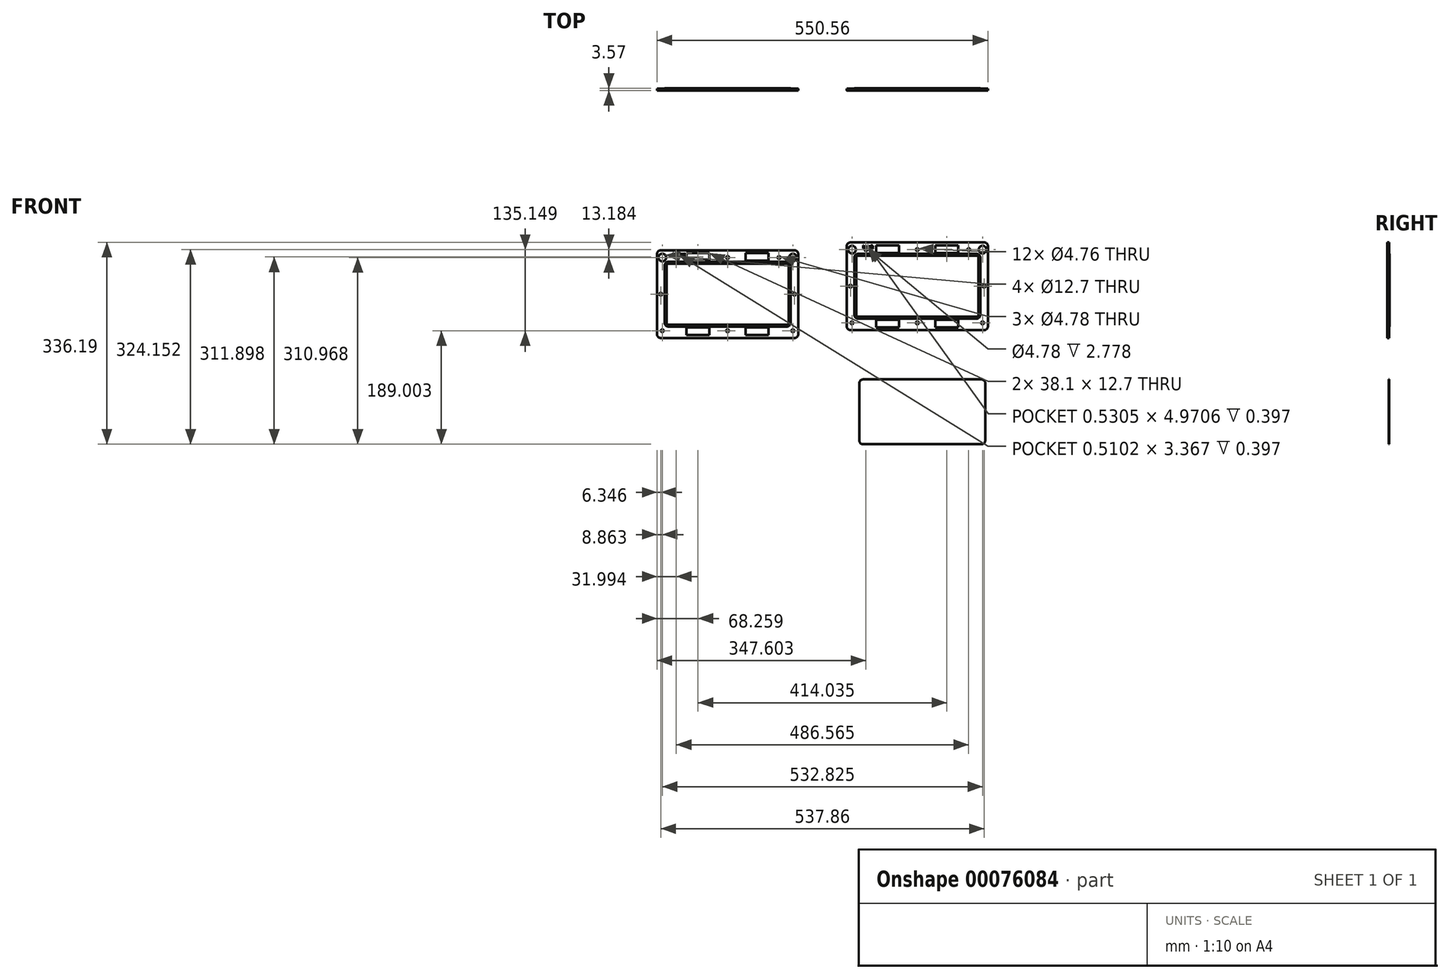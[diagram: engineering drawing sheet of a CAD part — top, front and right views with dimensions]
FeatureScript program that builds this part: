
annotation { "Feature Type Name" : "Feature", "Feature Type Description" : "" }
export const myFeature = defineFeature(function(context is Context, id is Id, definition is map)
    precondition{}
    {
        {
            var Q0;
            Q0=qCreatedBy(makeId("Front.planeOp"),FACE);
            var sketch = newSketch(context, id + "F0", { "sketchPlane" : qUnion([Q0])});
            skLineSegment(sketch, "E0.bottom", {"start": v(-85.43, 54.25) * mm, "end": v(111.42, 54.25) * mm});
            skLineSegment(sketch, "E0.top", {"start": v(-85.43, -53.7) * mm, "end": v(111.42, -53.7) * mm});
            skLineSegment(sketch, "E0.left", {"start": v(-91.78, 47.9) * mm, "end": v(-91.78, -47.35) * mm});
            skLineSegment(sketch, "E0.right", {"start": v(117.77, 47.9) * mm, "end": v(117.77, -47.35) * mm});
            skPoint(sketch, "E1.visualSharp", {"position": v(-91.78, 54.25) * mm});
            skArc(sketch, "E1.filletArc", {"start": v(-85.43, 54.25) * mm, "mid": v(-89.92, 52.4) * mm, "end": v(-91.78, 47.9) * mm});
            skPoint(sketch, "E2.visualSharp", {"position": v(117.77, 54.25) * mm});
            skArc(sketch, "E2.filletArc", {"start": v(117.77, 47.9) * mm, "mid": v(115.9, 52.4) * mm, "end": v(111.42, 54.25) * mm});
            skPoint(sketch, "E3.visualSharp", {"position": v(117.77, -53.7) * mm});
            skArc(sketch, "E3.filletArc", {"start": v(111.42, -53.7) * mm, "mid": v(115.9, -51.84) * mm, "end": v(117.77, -47.35) * mm});
            skPoint(sketch, "E4.visualSharp", {"position": v(-91.78, -53.7) * mm});
            skArc(sketch, "E4.filletArc", {"start": v(-91.78, -47.35) * mm, "mid": v(-89.92, -51.84) * mm, "end": v(-85.43, -53.7) * mm});
            skArc(sketch, "E5.0", {"start": v(-85.43, 51.08) * mm, "mid": v(-87.68, 50.15) * mm, "end": v(-88.6, 47.9) * mm});
            skLineSegment(sketch, "E5.1", {"start": v(-88.6, 47.9) * mm, "end": v(-88.6, -47.35) * mm});
            skLineSegment(sketch, "E5.2", {"start": v(-85.43, 51.08) * mm, "end": v(111.42, 51.08) * mm});
            skArc(sketch, "E5.3", {"start": v(-88.6, -47.35) * mm, "mid": v(-87.68, -49.6) * mm, "end": v(-85.43, -50.52) * mm});
            skArc(sketch, "E5.4", {"start": v(114.6, 47.9) * mm, "mid": v(113.66, 50.15) * mm, "end": v(111.42, 51.08) * mm});
            skLineSegment(sketch, "E5.5", {"start": v(114.6, 47.9) * mm, "end": v(114.6, -47.35) * mm});
            skArc(sketch, "E5.6", {"start": v(111.42, -50.52) * mm, "mid": v(113.66, -49.6) * mm, "end": v(114.6, -47.35) * mm});
            skLineSegment(sketch, "E5.7", {"start": v(-85.43, -50.52) * mm, "end": v(111.42, -50.52) * mm});
            skLineSegment(sketch, "E6.0", {"start": v(-98.13, 73.3) * mm, "end": v(124.12, 73.3) * mm});
            skLineSegment(sketch, "E7.0", {"start": v(-98.13, -72.75) * mm, "end": v(124.12, -72.75) * mm});
            skLineSegment(sketch, "E8.0", {"start": v(-104.48, 66.95) * mm, "end": v(-104.48, -66.4) * mm});
            skLineSegment(sketch, "E9.0", {"start": v(130.47, 66.95) * mm, "end": v(130.47, -66.4) * mm});
            skPoint(sketch, "E10.visualSharp", {"position": v(-104.48, 73.3) * mm});
            skArc(sketch, "E10.filletArc", {"start": v(-98.13, 73.3) * mm, "mid": v(-102.62, 71.44) * mm, "end": v(-104.48, 66.95) * mm});
            skPoint(sketch, "E11.visualSharp", {"position": v(130.47, 73.3) * mm});
            skArc(sketch, "E11.filletArc", {"start": v(130.47, 66.95) * mm, "mid": v(128.6, 71.44) * mm, "end": v(124.12, 73.3) * mm});
            skPoint(sketch, "E12.visualSharp", {"position": v(130.47, -72.75) * mm});
            skArc(sketch, "E12.filletArc", {"start": v(124.12, -72.75) * mm, "mid": v(128.6, -70.89) * mm, "end": v(130.47, -66.4) * mm});
            skPoint(sketch, "E13.visualSharp", {"position": v(-104.48, -72.75) * mm});
            skArc(sketch, "E13.filletArc", {"start": v(-104.48, -66.4) * mm, "mid": v(-102.62, -70.89) * mm, "end": v(-98.13, -72.75) * mm});
            skLineSegment(sketch, "E14", {"start": v(-104.48, 66.95) * mm, "end": v(-98.13, 73.3) * mm, "construction": true});
            skLineSegment(sketch, "E15", {"start": v(-101.3, 70.13) * mm, "end": v(-89.92, 52.4) * mm, "construction": true});
            skLineSegment(sketch, "E16", {"start": v(-104.48, 0.28) * mm, "end": v(-91.78, 0.28) * mm, "construction": true});
            skLineSegment(sketch, "E17", {"start": v(-98.13, -72.75) * mm, "end": v(-104.48, -66.4) * mm, "construction": true});
            skLineSegment(sketch, "E18", {"start": v(-101.3, -69.57) * mm, "end": v(-89.92, -51.84) * mm, "construction": true});
            skLineSegment(sketch, "E19", {"start": v(13, 94.6) * mm, "end": v(13, -140.03) * mm, "construction": true});
            skPoint(sketch, "E19.startSnap0", {"position": v(13, 73.3) * mm});
            skLineSegment(sketch, "E20", {"start": v(-149.83, 0.28) * mm, "end": v(205.44, 0.28) * mm, "construction": true});
            skLineSegment(sketch, "E21", {"start": v(-85.43, 54.25) * mm, "end": v(-85.43, 73.3) * mm, "construction": true});
            skCircle(sketch, "E22", {"center": v(-95.62, 61.26) * mm, "radius": 6.35 * mm});
            skCircle(sketch, "E23", {"center": v(-98.13, 0.28) * mm, "radius": 2.38 * mm});
            skCircle(sketch, "E24", {"center": v(-95.62, -60.7) * mm, "radius": 2.38 * mm});
            skLineSegment(sketch, "E25", {"start": v(-85.43, -53.7) * mm, "end": v(-85.43, -72.75) * mm, "construction": true});
            skLineSegment(sketch, "E26", {"start": v(-85.43, -72.75) * mm, "end": v(-85.43, -63.22) * mm, "construction": true});
            skLineSegment(sketch, "E27", {"start": v(-85.43, -63.22) * mm, "end": v(39.92, -63.22) * mm, "construction": true});
            skLineSegment(sketch, "E28", {"start": v(13, 54.25) * mm, "end": v(13, 73.3) * mm, "construction": true});
            skLineSegment(sketch, "E29", {"start": v(13, -72.75) * mm, "end": v(13, -53.7) * mm, "construction": true});
            skCircle(sketch, "E30", {"center": v(13, 61.26) * mm, "radius": 2.38 * mm});
            skLineSegment(sketch, "E31.bottom", {"start": v(-17.17, 55.84) * mm, "end": v(-55.27, 55.84) * mm});
            skLineSegment(sketch, "E31.top", {"start": v(-17.17, 68.54) * mm, "end": v(-55.27, 68.54) * mm});
            skLineSegment(sketch, "E31.left", {"start": v(-17.17, 55.84) * mm, "end": v(-17.17, 68.54) * mm});
            skLineSegment(sketch, "E31.right", {"start": v(-55.27, 55.84) * mm, "end": v(-55.27, 68.54) * mm});
            skPoint(sketch, "E31.middle", {"position": v(-36.22, 62.2) * mm});
            skLineSegment(sketch, "E32.MirrorCS", {"start": v(43.15, 55.84) * mm, "end": v(43.15, 68.54) * mm});
            skLineSegment(sketch, "E33.MirrorCS", {"start": v(43.15, 68.54) * mm, "end": v(81.25, 68.54) * mm});
            skLineSegment(sketch, "E34.MirrorCS", {"start": v(81.25, 55.84) * mm, "end": v(81.25, 68.54) * mm});
            skLineSegment(sketch, "E35.MirrorCS", {"start": v(43.15, 55.84) * mm, "end": v(81.25, 55.84) * mm});
            skCircle(sketch, "E36.MirrorC", {"center": v(121.6, 61.26) * mm, "radius": 6.35 * mm});
            skCircle(sketch, "E37.MirrorC", {"center": v(124.12, 0.28) * mm, "radius": 2.38 * mm});
            skCircle(sketch, "E38.MirrorC", {"center": v(121.6, -60.7) * mm, "radius": 2.38 * mm});
            skLineSegment(sketch, "E39.MirrorCS", {"start": v(-55.27, -55.28) * mm, "end": v(-55.27, -67.98) * mm});
            skLineSegment(sketch, "E40.MirrorCS", {"start": v(-17.17, -55.28) * mm, "end": v(-17.17, -67.98) * mm});
            skLineSegment(sketch, "E41.MirrorCS", {"start": v(-17.17, -55.28) * mm, "end": v(-55.27, -55.28) * mm});
            skLineSegment(sketch, "E42.MirrorCS", {"start": v(-17.17, -67.98) * mm, "end": v(-55.27, -67.98) * mm});
            skCircle(sketch, "E43.MirrorC", {"center": v(13, -60.7) * mm, "radius": 2.38 * mm});
            skLineSegment(sketch, "E44.MirrorCS", {"start": v(43.15, -55.28) * mm, "end": v(43.15, -67.98) * mm});
            skLineSegment(sketch, "E45.MirrorCS", {"start": v(43.15, -67.98) * mm, "end": v(81.25, -67.98) * mm});
            skLineSegment(sketch, "E46.MirrorCS", {"start": v(81.25, -55.28) * mm, "end": v(81.25, -67.98) * mm});
            skLineSegment(sketch, "E47.MirrorCS", {"start": v(43.15, -55.28) * mm, "end": v(81.25, -55.28) * mm});
            skLineSegment(sketch, "E48", {"start": v(-95.62, 61.26) * mm, "end": v(121.6, 61.26) * mm, "construction": true});
            skCircle(sketch, "E49", {"center": v(-72.49, 61.26) * mm, "radius": 2.39 * mm});
            skCircle(sketch, "E50", {"center": v(98.47, 61.26) * mm, "radius": 2.39 * mm});
            skSolve(sketch);
        }
        {
            var Q0;
            Q0 = qSketchRegion(id + "F0", true);
            var Q1;
            Q1=makeQuery(id+"F0.imprint","IMPRINT",FACE,{"disambiguationData":[TD([[makeQuery(id+"F0.imprint","IMPRINT",EDGE,{"derivedFrom":sQuery(id+"F0.wireOp",EDGE,"E0.bottom")}),-1.0]])]});
            extrude(context, id + "F1", {"entities" : qUnion([Q0, Q1]), "depth" : 0.8 * mm});
        }
        {
            var Q0;
            Q0=makeQuery(id+"F1.opExtrude","CAP_FACE",FACE,{"disambiguationData":[OSD([sQuery(id+"F0.wireOp",EDGE,"E5.0"),sQuery(id+"F0.wireOp",EDGE,"E5.1"),sQuery(id+"F0.wireOp",EDGE,"E5.2"),sQuery(id+"F0.wireOp",EDGE,"E5.3"),sQuery(id+"F0.wireOp",EDGE,"E5.4"),sQuery(id+"F0.wireOp",EDGE,"E5.5"),sQuery(id+"F0.wireOp",EDGE,"E5.6"),sQuery(id+"F0.wireOp",EDGE,"E5.7"),sQuery(id+"F0.wireOp",EDGE,"E6.0"),sQuery(id+"F0.wireOp",EDGE,"E7.0"),sQuery(id+"F0.wireOp",EDGE,"E8.0"),sQuery(id+"F0.wireOp",EDGE,"E9.0"),sQuery(id+"F0.wireOp",EDGE,"E10.filletArc"),sQuery(id+"F0.wireOp",EDGE,"E11.filletArc"),sQuery(id+"F0.wireOp",EDGE,"E12.filletArc"),sQuery(id+"F0.wireOp",EDGE,"E13.filletArc"),sQuery(id+"F0.wireOp",EDGE,"E22"),sQuery(id+"F0.wireOp",EDGE,"E23"),sQuery(id+"F0.wireOp",EDGE,"E24"),sQuery(id+"F0.wireOp",EDGE,"E30"),sQuery(id+"F0.wireOp",EDGE,"E31.bottom"),sQuery(id+"F0.wireOp",EDGE,"E31.top"),sQuery(id+"F0.wireOp",EDGE,"E31.left"),sQuery(id+"F0.wireOp",EDGE,"E31.right"),sQuery(id+"F0.wireOp",EDGE,"E32.MirrorCS"),sQuery(id+"F0.wireOp",EDGE,"E33.MirrorCS"),sQuery(id+"F0.wireOp",EDGE,"E34.MirrorCS"),sQuery(id+"F0.wireOp",EDGE,"E35.MirrorCS"),sQuery(id+"F0.wireOp",EDGE,"E36.MirrorC"),sQuery(id+"F0.wireOp",EDGE,"E37.MirrorC"),sQuery(id+"F0.wireOp",EDGE,"E38.MirrorC"),sQuery(id+"F0.wireOp",EDGE,"E39.MirrorCS"),sQuery(id+"F0.wireOp",EDGE,"E40.MirrorCS"),sQuery(id+"F0.wireOp",EDGE,"E41.MirrorCS"),sQuery(id+"F0.wireOp",EDGE,"E42.MirrorCS"),sQuery(id+"F0.wireOp",EDGE,"E43.MirrorC"),sQuery(id+"F0.wireOp",EDGE,"E44.MirrorCS"),sQuery(id+"F0.wireOp",EDGE,"E45.MirrorCS"),sQuery(id+"F0.wireOp",EDGE,"E46.MirrorCS"),sQuery(id+"F0.wireOp",EDGE,"E47.MirrorCS")])],"isStart":false});
            var sketch = newSketch(context, id + "F2", { "sketchPlane" : qUnion([Q0])});
            skLineSegment(sketch, "E51.0", {"start": v(-85.43, 54.25) * mm, "end": v(111.42, 54.25) * mm});
            skLineSegment(sketch, "E52.0", {"start": v(-85.43, -53.7) * mm, "end": v(111.42, -53.7) * mm});
            skLineSegment(sketch, "E53", {"start": v(-91.78, 47.9) * mm, "end": v(-91.78, -47.35) * mm});
            skLineSegment(sketch, "E54", {"start": v(117.77, 47.9) * mm, "end": v(117.77, -47.35) * mm});
            skPoint(sketch, "E55.visualSharp", {"position": v(-91.78, 54.25) * mm});
            skArc(sketch, "E55.filletArc", {"start": v(-85.43, 54.25) * mm, "mid": v(-89.92, 52.4) * mm, "end": v(-91.78, 47.9) * mm});
            skPoint(sketch, "E56.visualSharp", {"position": v(117.77, 54.25) * mm});
            skArc(sketch, "E56.filletArc", {"start": v(117.77, 47.9) * mm, "mid": v(115.9, 52.4) * mm, "end": v(111.42, 54.25) * mm});
            skPoint(sketch, "E57.visualSharp", {"position": v(117.77, -53.7) * mm});
            skArc(sketch, "E57.filletArc", {"start": v(111.42, -53.7) * mm, "mid": v(115.9, -51.84) * mm, "end": v(117.77, -47.35) * mm});
            skPoint(sketch, "E58.visualSharp", {"position": v(-91.78, -53.7) * mm});
            skArc(sketch, "E58.filletArc", {"start": v(-91.78, -47.35) * mm, "mid": v(-89.92, -51.84) * mm, "end": v(-85.43, -53.7) * mm});
            skSolve(sketch);
        }
        {
            var Q0;
            Q0=makeQuery(id+"F2.imprint","IMPRINT",FACE,{"disambiguationData":[TD([[makeQuery(id+"F2.imprint","IMPRINT",EDGE,{"derivedFrom":sQuery(id+"F2.wireOp",EDGE,"E51.0")}),1.0]])]});
            extrude(context, id + "F3", {"entities" : qUnion([Q0]), "operationType" : NewBodyOperationType.ADD, "depth" : 1.98 * mm});
        }
        {
            var Q0;
            Q0=qCreatedBy(makeId("Front.planeOp"),FACE);
            var sketch = newSketch(context, id + "F4", { "sketchPlane" : qUnion([Q0])});
            skLineSegment(sketch, "E59.bottom", {"start": v(-77.21, -154.94) * mm, "end": v(119.64, -154.94) * mm});
            skLineSegment(sketch, "E59.top", {"start": v(-77.21, -262.89) * mm, "end": v(119.64, -262.89) * mm});
            skLineSegment(sketch, "E59.left", {"start": v(-83.56, -161.29) * mm, "end": v(-83.56, -256.54) * mm});
            skLineSegment(sketch, "E59.right", {"start": v(125.99, -161.29) * mm, "end": v(125.99, -256.54) * mm});
            skPoint(sketch, "E60.visualSharp", {"position": v(-83.56, -154.94) * mm});
            skArc(sketch, "E60.filletArc", {"start": v(-77.21, -154.94) * mm, "mid": v(-81.7, -156.8) * mm, "end": v(-83.56, -161.29) * mm});
            skPoint(sketch, "E61.visualSharp", {"position": v(125.99, -154.94) * mm});
            skArc(sketch, "E61.filletArc", {"start": v(125.99, -161.29) * mm, "mid": v(124.13, -156.8) * mm, "end": v(119.64, -154.94) * mm});
            skPoint(sketch, "E62.visualSharp", {"position": v(-83.56, -262.89) * mm});
            skArc(sketch, "E62.filletArc", {"start": v(-83.56, -256.54) * mm, "mid": v(-81.7, -261.03) * mm, "end": v(-77.21, -262.89) * mm});
            skPoint(sketch, "E63.visualSharp", {"position": v(125.99, -262.89) * mm});
            skArc(sketch, "E63.filletArc", {"start": v(119.64, -262.89) * mm, "mid": v(124.13, -261.03) * mm, "end": v(125.99, -256.54) * mm});
            skSolve(sketch);
        }
        {
            var Q0;
            Q0 = qSketchRegion(id + "F4", true);
            extrude(context, id + "F5", {"entities" : qUnion([Q0]), "depth" : 0.4 * mm});
        }
        {
            var Q0;
            Q0=makeQuery(id+"F1.opExtrude","CAP_FACE",FACE,{"disambiguationData":[OSD([sQuery(id+"F0.wireOp",EDGE,"E5.0"),sQuery(id+"F0.wireOp",EDGE,"E5.1"),sQuery(id+"F0.wireOp",EDGE,"E5.2"),sQuery(id+"F0.wireOp",EDGE,"E5.3"),sQuery(id+"F0.wireOp",EDGE,"E5.4"),sQuery(id+"F0.wireOp",EDGE,"E5.5"),sQuery(id+"F0.wireOp",EDGE,"E5.6"),sQuery(id+"F0.wireOp",EDGE,"E5.7"),sQuery(id+"F0.wireOp",EDGE,"E6.0"),sQuery(id+"F0.wireOp",EDGE,"E7.0"),sQuery(id+"F0.wireOp",EDGE,"E8.0"),sQuery(id+"F0.wireOp",EDGE,"E9.0"),sQuery(id+"F0.wireOp",EDGE,"E10.filletArc"),sQuery(id+"F0.wireOp",EDGE,"E11.filletArc"),sQuery(id+"F0.wireOp",EDGE,"E12.filletArc"),sQuery(id+"F0.wireOp",EDGE,"E13.filletArc"),sQuery(id+"F0.wireOp",EDGE,"E22"),sQuery(id+"F0.wireOp",EDGE,"E23"),sQuery(id+"F0.wireOp",EDGE,"E24"),sQuery(id+"F0.wireOp",EDGE,"E30"),sQuery(id+"F0.wireOp",EDGE,"E31.bottom"),sQuery(id+"F0.wireOp",EDGE,"E31.top"),sQuery(id+"F0.wireOp",EDGE,"E31.left"),sQuery(id+"F0.wireOp",EDGE,"E31.right"),sQuery(id+"F0.wireOp",EDGE,"E32.MirrorCS"),sQuery(id+"F0.wireOp",EDGE,"E33.MirrorCS"),sQuery(id+"F0.wireOp",EDGE,"E34.MirrorCS"),sQuery(id+"F0.wireOp",EDGE,"E35.MirrorCS"),sQuery(id+"F0.wireOp",EDGE,"E36.MirrorC"),sQuery(id+"F0.wireOp",EDGE,"E37.MirrorC"),sQuery(id+"F0.wireOp",EDGE,"E38.MirrorC"),sQuery(id+"F0.wireOp",EDGE,"E39.MirrorCS"),sQuery(id+"F0.wireOp",EDGE,"E40.MirrorCS"),sQuery(id+"F0.wireOp",EDGE,"E41.MirrorCS"),sQuery(id+"F0.wireOp",EDGE,"E42.MirrorCS"),sQuery(id+"F0.wireOp",EDGE,"E43.MirrorC"),sQuery(id+"F0.wireOp",EDGE,"E44.MirrorCS"),sQuery(id+"F0.wireOp",EDGE,"E45.MirrorCS"),sQuery(id+"F0.wireOp",EDGE,"E46.MirrorCS"),sQuery(id+"F0.wireOp",EDGE,"E47.MirrorCS")])],"isStart":true});
            var sketch = newSketch(context, id + "F6", { "sketchPlane" : qUnion([Q0])});
            skLineSegment(sketch, "E64.0", {"start": v(85.43, 54.25) * mm, "end": v(55.27, 54.25) * mm});
            skArc(sketch, "E64.1", {"start": v(85.43, 54.25) * mm, "mid": v(89.92, 52.4) * mm, "end": v(91.78, 47.9) * mm});
            skLineSegment(sketch, "E64.2", {"start": v(91.78, 47.9) * mm, "end": v(91.78, -47.35) * mm});
            skArc(sketch, "E64.3", {"start": v(91.78, -47.35) * mm, "mid": v(89.92, -51.84) * mm, "end": v(85.43, -53.7) * mm});
            skLineSegment(sketch, "E64.4", {"start": v(85.43, -53.7) * mm, "end": v(-111.42, -53.7) * mm});
            skLineSegment(sketch, "E64.5", {"start": v(17.17, 54.25) * mm, "end": v(-111.42, 54.25) * mm});
            skArc(sketch, "E64.6", {"start": v(-117.77, 47.9) * mm, "mid": v(-115.9, 52.4) * mm, "end": v(-111.42, 54.25) * mm});
            skLineSegment(sketch, "E64.7", {"start": v(-117.77, 47.9) * mm, "end": v(-117.77, -47.35) * mm});
            skArc(sketch, "E64.8", {"start": v(-111.42, -53.7) * mm, "mid": v(-115.9, -51.84) * mm, "end": v(-117.77, -47.35) * mm});
            skLineSegment(sketch, "E65", {"start": v(17.17, 54.25) * mm, "end": v(55.27, 54.25) * mm});
            skArc(sketch, "E66.0", {"start": v(85.43, 51.08) * mm, "mid": v(87.68, 50.15) * mm, "end": v(88.6, 47.9) * mm});
            skLineSegment(sketch, "E66.1", {"start": v(88.6, 47.9) * mm, "end": v(88.6, -47.35) * mm});
            skLineSegment(sketch, "E66.2", {"start": v(85.43, 51.08) * mm, "end": v(-111.42, 51.08) * mm});
            skArc(sketch, "E66.3", {"start": v(88.6, -47.35) * mm, "mid": v(87.68, -49.6) * mm, "end": v(85.43, -50.52) * mm});
            skArc(sketch, "E66.4", {"start": v(-114.6, 47.9) * mm, "mid": v(-113.66, 50.15) * mm, "end": v(-111.42, 51.08) * mm});
            skLineSegment(sketch, "E66.5", {"start": v(-114.6, 47.9) * mm, "end": v(-114.6, -47.35) * mm});
            skArc(sketch, "E66.6", {"start": v(-111.42, -50.52) * mm, "mid": v(-113.66, -49.6) * mm, "end": v(-114.6, -47.35) * mm});
            skLineSegment(sketch, "E66.7", {"start": v(85.43, -50.52) * mm, "end": v(-111.42, -50.52) * mm});
            skSolve(sketch);
        }
        {
            var Q0;
            Q0 = qSketchRegion(id + "F6", true);
            extrude(context, id + "F7", {"entities" : qUnion([Q0]), "operationType" : NewBodyOperationType.ADD, "depth" : 0.8 * mm});
        }
        {
            var Q0;
            Q0=makeQuery(id+"F0.imprint","IMPRINT",FACE,{"disambiguationData":[TD([[makeQuery(id+"F0.imprint","IMPRINT",EDGE,{"derivedFrom":sQuery(id+"F0.wireOp",EDGE,"E0.bottom")}),1.0]])]});
            var sketch = newSketch(context, id + "F8", { "sketchPlane" : qUnion([Q0])});
            skLineSegment(sketch, "E67.bottom", {"start": v(-17.17, 55.84) * mm, "end": v(-55.3, 55.84) * mm});
            skLineSegment(sketch, "E67.top", {"start": v(-17.17, 50.55) * mm, "end": v(-55.3, 50.55) * mm});
            skLineSegment(sketch, "E67.left", {"start": v(-17.17, 55.84) * mm, "end": v(-17.17, 50.55) * mm});
            skLineSegment(sketch, "E67.right", {"start": v(-55.3, 55.84) * mm, "end": v(-55.3, 50.55) * mm});
            skLineSegment(sketch, "E68.MirrorCS", {"start": v(-17.17, -55.28) * mm, "end": v(-55.3, -55.28) * mm});
            skLineSegment(sketch, "E69.MirrorCS", {"start": v(-17.17, -55.28) * mm, "end": v(-17.17, -49.99) * mm});
            skLineSegment(sketch, "E70.MirrorCS", {"start": v(-17.17, -49.99) * mm, "end": v(-55.3, -49.99) * mm});
            skLineSegment(sketch, "E71.MirrorCS", {"start": v(-55.3, -55.28) * mm, "end": v(-55.3, -49.99) * mm});
            skLineSegment(sketch, "E72.MirrorCS", {"start": v(43.15, -55.28) * mm, "end": v(43.15, -49.99) * mm});
            skLineSegment(sketch, "E73.MirrorCS", {"start": v(43.15, -49.99) * mm, "end": v(81.27, -49.99) * mm});
            skLineSegment(sketch, "E74.MirrorCS", {"start": v(43.15, -55.28) * mm, "end": v(81.27, -55.28) * mm});
            skLineSegment(sketch, "E75.MirrorCS", {"start": v(81.27, -55.28) * mm, "end": v(81.27, -49.99) * mm});
            skSolve(sketch);
        }
        {
            var Q0;
            Q0 = qSketchRegion(id + "F8", true);
            extrude(context, id + "F9", {"entities" : qUnion([Q0]), "operationType" : NewBodyOperationType.REMOVE, "depth" : 0.8 * mm});
        }
        {
            var Q0;
            Q0=makeQuery(id+"F3.opExtrude","CAP_FACE",FACE,{"disambiguationData":[OSD([sQuery(id+"F0.wireOp",EDGE,"E6.0"),sQuery(id+"F0.wireOp",EDGE,"E7.0"),sQuery(id+"F0.wireOp",EDGE,"E8.0"),sQuery(id+"F0.wireOp",EDGE,"E9.0"),sQuery(id+"F0.wireOp",EDGE,"E10.filletArc"),sQuery(id+"F0.wireOp",EDGE,"E11.filletArc"),sQuery(id+"F0.wireOp",EDGE,"E12.filletArc"),sQuery(id+"F0.wireOp",EDGE,"E13.filletArc"),sQuery(id+"F0.wireOp",EDGE,"E22"),sQuery(id+"F0.wireOp",EDGE,"E23"),sQuery(id+"F0.wireOp",EDGE,"E24"),sQuery(id+"F0.wireOp",EDGE,"E30"),sQuery(id+"F0.wireOp",EDGE,"E31.bottom"),sQuery(id+"F0.wireOp",EDGE,"E31.top"),sQuery(id+"F0.wireOp",EDGE,"E31.left"),sQuery(id+"F0.wireOp",EDGE,"E31.right"),sQuery(id+"F0.wireOp",EDGE,"E32.MirrorCS"),sQuery(id+"F0.wireOp",EDGE,"E33.MirrorCS"),sQuery(id+"F0.wireOp",EDGE,"E34.MirrorCS"),sQuery(id+"F0.wireOp",EDGE,"E35.MirrorCS"),sQuery(id+"F0.wireOp",EDGE,"E36.MirrorC"),sQuery(id+"F0.wireOp",EDGE,"E37.MirrorC"),sQuery(id+"F0.wireOp",EDGE,"E38.MirrorC"),sQuery(id+"F0.wireOp",EDGE,"E39.MirrorCS"),sQuery(id+"F0.wireOp",EDGE,"E40.MirrorCS"),sQuery(id+"F0.wireOp",EDGE,"E41.MirrorCS"),sQuery(id+"F0.wireOp",EDGE,"E42.MirrorCS"),sQuery(id+"F0.wireOp",EDGE,"E43.MirrorC"),sQuery(id+"F0.wireOp",EDGE,"E44.MirrorCS"),sQuery(id+"F0.wireOp",EDGE,"E45.MirrorCS"),sQuery(id+"F0.wireOp",EDGE,"E46.MirrorCS"),sQuery(id+"F0.wireOp",EDGE,"E47.MirrorCS"),sQuery(id+"F2.wireOp",EDGE,"E51.0"),sQuery(id+"F2.wireOp",EDGE,"E52.0"),sQuery(id+"F2.wireOp",EDGE,"E53"),sQuery(id+"F2.wireOp",EDGE,"E54"),sQuery(id+"F2.wireOp",EDGE,"E55.filletArc"),sQuery(id+"F2.wireOp",EDGE,"E56.filletArc"),sQuery(id+"F2.wireOp",EDGE,"E57.filletArc"),sQuery(id+"F2.wireOp",EDGE,"E58.filletArc")])],"isStart":false});
            var sketch = newSketch(context, id + "F10", { "sketchPlane" : qUnion([Q0])});
            skText(sketch, "E76", { "text": "M left", "fontName": "OpenSans-Regular.ttf"});
            const initialGuessF10  = {"E76": [-0.07783, 0.06345, 1, 0, 0.00471]};
            skSetInitialGuess(sketch, initialGuessF10);
            skSolve(sketch);
        }
        {
            var Q0;
            Q0 = qSketchRegion(id + "F10", true);
            extrude(context, id + "F11", {"entities" : qUnion([Q0]), "operationType" : NewBodyOperationType.REMOVE, "oppositeDirection" : true, "depth" : 0.4 * mm});
        }
        {
            var Q0;
            Q0=qCreatedBy(makeId("Front.planeOp"),FACE);
            var sketch = newSketch(context, id + "F12", { "sketchPlane" : qUnion([Q0])});
            skLineSegment(sketch, "E77.bottom", {"start": v(-401.04, 41.07) * mm, "end": v(-204.2, 41.07) * mm});
            skLineSegment(sketch, "E77.top", {"start": v(-401.04, -66.88) * mm, "end": v(-204.2, -66.88) * mm});
            skLineSegment(sketch, "E77.left", {"start": v(-407.4, 34.72) * mm, "end": v(-407.4, -60.53) * mm});
            skLineSegment(sketch, "E77.right", {"start": v(-197.84, 34.72) * mm, "end": v(-197.84, -60.53) * mm});
            skPoint(sketch, "E78.visualSharp", {"position": v(-407.4, 41.07) * mm});
            skArc(sketch, "E78.filletArc", {"start": v(-401.04, 41.07) * mm, "mid": v(-405.53, 39.21) * mm, "end": v(-407.4, 34.72) * mm});
            skPoint(sketch, "E79.visualSharp", {"position": v(-197.84, 41.07) * mm});
            skArc(sketch, "E79.filletArc", {"start": v(-197.84, 34.72) * mm, "mid": v(-199.7, 39.21) * mm, "end": v(-204.2, 41.07) * mm});
            skPoint(sketch, "E80.visualSharp", {"position": v(-197.84, -66.88) * mm});
            skArc(sketch, "E80.filletArc", {"start": v(-204.2, -66.88) * mm, "mid": v(-199.7, -65.02) * mm, "end": v(-197.84, -60.53) * mm});
            skPoint(sketch, "E81.visualSharp", {"position": v(-407.4, -66.88) * mm});
            skArc(sketch, "E81.filletArc", {"start": v(-407.4, -60.53) * mm, "mid": v(-405.53, -65.02) * mm, "end": v(-401.04, -66.88) * mm});
            skArc(sketch, "E82.0", {"start": v(-401.04, 37.9) * mm, "mid": v(-403.29, 36.97) * mm, "end": v(-404.22, 34.72) * mm});
            skLineSegment(sketch, "E82.1", {"start": v(-404.22, 34.72) * mm, "end": v(-404.22, -60.53) * mm});
            skLineSegment(sketch, "E82.2", {"start": v(-401.04, 37.9) * mm, "end": v(-204.2, 37.9) * mm});
            skArc(sketch, "E82.3", {"start": v(-404.22, -60.53) * mm, "mid": v(-403.29, -62.77) * mm, "end": v(-401.04, -63.7) * mm});
            skArc(sketch, "E82.4", {"start": v(-201.02, 34.72) * mm, "mid": v(-201.95, 36.97) * mm, "end": v(-204.2, 37.9) * mm});
            skLineSegment(sketch, "E82.5", {"start": v(-201.02, 34.72) * mm, "end": v(-201.02, -60.53) * mm});
            skArc(sketch, "E82.6", {"start": v(-204.2, -63.7) * mm, "mid": v(-201.95, -62.77) * mm, "end": v(-201.02, -60.53) * mm});
            skLineSegment(sketch, "E82.7", {"start": v(-401.04, -63.7) * mm, "end": v(-204.2, -63.7) * mm});
            skLineSegment(sketch, "E83.0", {"start": v(-413.74, 60.12) * mm, "end": v(-191.5, 60.12) * mm});
            skLineSegment(sketch, "E84.0", {"start": v(-413.74, -85.93) * mm, "end": v(-191.5, -85.93) * mm});
            skLineSegment(sketch, "E85.0", {"start": v(-420.1, 53.77) * mm, "end": v(-420.1, -79.58) * mm});
            skLineSegment(sketch, "E86.0", {"start": v(-185.14, 53.77) * mm, "end": v(-185.14, -79.58) * mm});
            skPoint(sketch, "E87.visualSharp", {"position": v(-420.1, 60.12) * mm});
            skArc(sketch, "E87.filletArc", {"start": v(-413.74, 60.12) * mm, "mid": v(-418.23, 58.26) * mm, "end": v(-420.1, 53.77) * mm});
            skPoint(sketch, "E88.visualSharp", {"position": v(-185.14, 60.12) * mm});
            skArc(sketch, "E88.filletArc", {"start": v(-185.14, 53.77) * mm, "mid": v(-187, 58.26) * mm, "end": v(-191.5, 60.12) * mm});
            skPoint(sketch, "E89.visualSharp", {"position": v(-185.14, -85.93) * mm});
            skArc(sketch, "E89.filletArc", {"start": v(-191.5, -85.93) * mm, "mid": v(-187, -84.07) * mm, "end": v(-185.14, -79.58) * mm});
            skPoint(sketch, "E90.visualSharp", {"position": v(-420.1, -85.93) * mm});
            skArc(sketch, "E90.filletArc", {"start": v(-420.1, -79.58) * mm, "mid": v(-418.23, -84.07) * mm, "end": v(-413.74, -85.93) * mm});
            skLineSegment(sketch, "E91", {"start": v(-420.1, 53.77) * mm, "end": v(-413.74, 60.12) * mm, "construction": true});
            skLineSegment(sketch, "E92", {"start": v(-416.92, 56.95) * mm, "end": v(-405.53, 39.21) * mm, "construction": true});
            skLineSegment(sketch, "E93", {"start": v(-420.1, -12.9) * mm, "end": v(-407.4, -12.9) * mm, "construction": true});
            skLineSegment(sketch, "E94", {"start": v(-413.74, -85.93) * mm, "end": v(-420.1, -79.58) * mm, "construction": true});
            skLineSegment(sketch, "E95", {"start": v(-416.92, -82.75) * mm, "end": v(-405.53, -65.02) * mm, "construction": true});
            skLineSegment(sketch, "E96", {"start": v(-302.62, 81.4) * mm, "end": v(-302.62, -153.21) * mm, "construction": true});
            skPoint(sketch, "E96.startSnap0", {"position": v(-302.62, 60.12) * mm});
            skLineSegment(sketch, "E97", {"start": v(-465.44, -12.9) * mm, "end": v(-110.17, -12.9) * mm, "construction": true});
            skLineSegment(sketch, "E98", {"start": v(-401.04, 41.07) * mm, "end": v(-401.04, 60.12) * mm, "construction": true});
            skCircle(sketch, "E99", {"center": v(-411.23, 48.08) * mm, "radius": 6.35 * mm});
            skCircle(sketch, "E100", {"center": v(-413.74, -12.9) * mm, "radius": 2.38 * mm});
            skCircle(sketch, "E101", {"center": v(-411.23, -73.89) * mm, "radius": 2.38 * mm});
            skLineSegment(sketch, "E102", {"start": v(-401.04, -66.88) * mm, "end": v(-401.04, -85.93) * mm, "construction": true});
            skLineSegment(sketch, "E103", {"start": v(-401.04, -85.93) * mm, "end": v(-401.04, -76.4) * mm, "construction": true});
            skLineSegment(sketch, "E104", {"start": v(-401.04, -76.4) * mm, "end": v(-275.69, -76.4) * mm, "construction": true});
            skLineSegment(sketch, "E105", {"start": v(-302.62, 41.07) * mm, "end": v(-302.62, 60.12) * mm, "construction": true});
            skLineSegment(sketch, "E106", {"start": v(-302.62, -85.93) * mm, "end": v(-302.62, -66.88) * mm, "construction": true});
            skCircle(sketch, "E107", {"center": v(-302.61, 48.08) * mm, "radius": 2.38 * mm});
            skLineSegment(sketch, "E108.bottom", {"start": v(-332.78, 42.66) * mm, "end": v(-370.88, 42.66) * mm});
            skLineSegment(sketch, "E108.top", {"start": v(-332.78, 55.36) * mm, "end": v(-370.88, 55.36) * mm});
            skLineSegment(sketch, "E108.left", {"start": v(-332.78, 42.66) * mm, "end": v(-332.78, 55.36) * mm});
            skLineSegment(sketch, "E108.right", {"start": v(-370.88, 42.66) * mm, "end": v(-370.88, 55.36) * mm});
            skPoint(sketch, "E108.middle", {"position": v(-351.83, 49) * mm});
            skLineSegment(sketch, "E109.MirrorCS", {"start": v(-272.46, 42.66) * mm, "end": v(-272.46, 55.36) * mm});
            skLineSegment(sketch, "E110.MirrorCS", {"start": v(-272.46, 55.36) * mm, "end": v(-234.36, 55.36) * mm});
            skLineSegment(sketch, "E111.MirrorCS", {"start": v(-234.36, 42.66) * mm, "end": v(-234.36, 55.36) * mm});
            skLineSegment(sketch, "E112.MirrorCS", {"start": v(-272.46, 42.66) * mm, "end": v(-234.36, 42.66) * mm});
            skCircle(sketch, "E113.MirrorC", {"center": v(-194.01, 48.08) * mm, "radius": 6.35 * mm});
            skCircle(sketch, "E114.MirrorC", {"center": v(-191.5, -12.9) * mm, "radius": 2.38 * mm});
            skCircle(sketch, "E115.MirrorC", {"center": v(-194.01, -73.89) * mm, "radius": 2.38 * mm});
            skLineSegment(sketch, "E116.MirrorCS", {"start": v(-370.88, -68.47) * mm, "end": v(-370.88, -81.17) * mm});
            skLineSegment(sketch, "E117.MirrorCS", {"start": v(-332.78, -68.47) * mm, "end": v(-332.78, -81.17) * mm});
            skLineSegment(sketch, "E118.MirrorCS", {"start": v(-332.78, -68.47) * mm, "end": v(-370.88, -68.47) * mm});
            skLineSegment(sketch, "E119.MirrorCS", {"start": v(-332.78, -81.17) * mm, "end": v(-370.88, -81.17) * mm});
            skCircle(sketch, "E120.MirrorC", {"center": v(-302.61, -73.89) * mm, "radius": 2.38 * mm});
            skLineSegment(sketch, "E121.MirrorCS", {"start": v(-272.46, -68.47) * mm, "end": v(-272.46, -81.17) * mm});
            skLineSegment(sketch, "E122.MirrorCS", {"start": v(-272.46, -81.17) * mm, "end": v(-234.36, -81.17) * mm});
            skLineSegment(sketch, "E123.MirrorCS", {"start": v(-234.36, -68.47) * mm, "end": v(-234.36, -81.17) * mm});
            skLineSegment(sketch, "E124.MirrorCS", {"start": v(-272.46, -68.47) * mm, "end": v(-234.36, -68.47) * mm});
            skLineSegment(sketch, "E125", {"start": v(-411.23, 48.08) * mm, "end": v(-194.01, 48.08) * mm, "construction": true});
            skCircle(sketch, "E126", {"center": v(-388.1, 48.08) * mm, "radius": 2.39 * mm});
            skCircle(sketch, "E127", {"center": v(-217.14, 48.08) * mm, "radius": 2.39 * mm});
            skSolve(sketch);
        }
        {
            var Q0;
            Q0 = qSketchRegion(id + "F12", true);
            var Q1;
            Q1=makeQuery(id+"F12.imprint","IMPRINT",FACE,{"disambiguationData":[TD([[makeQuery(id+"F12.imprint","IMPRINT",EDGE,{"derivedFrom":sQuery(id+"F12.wireOp",EDGE,"E77.bottom")}),-1.0]])]});
            extrude(context, id + "F13", {"entities" : qUnion([Q0, Q1]), "depth" : 0.8 * mm});
        }
        {
            var Q0;
            Q0=makeQuery(id+"F13.opExtrude","CAP_FACE",FACE,{"disambiguationData":[OSD([sQuery(id+"F12.wireOp",EDGE,"E82.0"),sQuery(id+"F12.wireOp",EDGE,"E82.1"),sQuery(id+"F12.wireOp",EDGE,"E82.2"),sQuery(id+"F12.wireOp",EDGE,"E82.3"),sQuery(id+"F12.wireOp",EDGE,"E82.4"),sQuery(id+"F12.wireOp",EDGE,"E82.5"),sQuery(id+"F12.wireOp",EDGE,"E82.6"),sQuery(id+"F12.wireOp",EDGE,"E82.7"),sQuery(id+"F12.wireOp",EDGE,"E83.0"),sQuery(id+"F12.wireOp",EDGE,"E84.0"),sQuery(id+"F12.wireOp",EDGE,"E85.0"),sQuery(id+"F12.wireOp",EDGE,"E86.0"),sQuery(id+"F12.wireOp",EDGE,"E87.filletArc"),sQuery(id+"F12.wireOp",EDGE,"E88.filletArc"),sQuery(id+"F12.wireOp",EDGE,"E89.filletArc"),sQuery(id+"F12.wireOp",EDGE,"E90.filletArc"),sQuery(id+"F12.wireOp",EDGE,"E99"),sQuery(id+"F12.wireOp",EDGE,"E100"),sQuery(id+"F12.wireOp",EDGE,"E101"),sQuery(id+"F12.wireOp",EDGE,"E107"),sQuery(id+"F12.wireOp",EDGE,"E108.bottom"),sQuery(id+"F12.wireOp",EDGE,"E108.top"),sQuery(id+"F12.wireOp",EDGE,"E108.left"),sQuery(id+"F12.wireOp",EDGE,"E108.right"),sQuery(id+"F12.wireOp",EDGE,"E109.MirrorCS"),sQuery(id+"F12.wireOp",EDGE,"E110.MirrorCS"),sQuery(id+"F12.wireOp",EDGE,"E111.MirrorCS"),sQuery(id+"F12.wireOp",EDGE,"E112.MirrorCS"),sQuery(id+"F12.wireOp",EDGE,"E113.MirrorC"),sQuery(id+"F12.wireOp",EDGE,"E114.MirrorC"),sQuery(id+"F12.wireOp",EDGE,"E115.MirrorC"),sQuery(id+"F12.wireOp",EDGE,"E116.MirrorCS"),sQuery(id+"F12.wireOp",EDGE,"E117.MirrorCS"),sQuery(id+"F12.wireOp",EDGE,"E118.MirrorCS"),sQuery(id+"F12.wireOp",EDGE,"E119.MirrorCS"),sQuery(id+"F12.wireOp",EDGE,"E120.MirrorC"),sQuery(id+"F12.wireOp",EDGE,"E121.MirrorCS"),sQuery(id+"F12.wireOp",EDGE,"E122.MirrorCS"),sQuery(id+"F12.wireOp",EDGE,"E123.MirrorCS"),sQuery(id+"F12.wireOp",EDGE,"E124.MirrorCS")])],"isStart":false});
            var sketch = newSketch(context, id + "F14", { "sketchPlane" : qUnion([Q0])});
            skLineSegment(sketch, "E128", {"start": v(-401.04, 37.9) * mm, "end": v(-204.2, 37.9) * mm, "construction": true});
            skLineSegment(sketch, "E129", {"start": v(-204.2, -63.7) * mm, "end": v(-401.04, -63.7) * mm, "construction": true});
            skArc(sketch, "E130.0", {"start": v(-401.04, 41.07) * mm, "mid": v(-405.53, 39.21) * mm, "end": v(-407.4, 34.72) * mm});
            skLineSegment(sketch, "E130.1", {"start": v(-407.4, 34.72) * mm, "end": v(-407.4, -60.53) * mm});
            skLineSegment(sketch, "E130.2", {"start": v(-401.04, 41.07) * mm, "end": v(-204.2, 41.07) * mm});
            skArc(sketch, "E130.3", {"start": v(-407.4, -60.53) * mm, "mid": v(-405.53, -65.02) * mm, "end": v(-401.04, -66.88) * mm});
            skArc(sketch, "E130.4", {"start": v(-197.84, 34.72) * mm, "mid": v(-199.7, 39.21) * mm, "end": v(-204.2, 41.07) * mm});
            skLineSegment(sketch, "E130.5", {"start": v(-197.84, 34.72) * mm, "end": v(-197.84, -60.53) * mm});
            skArc(sketch, "E130.6", {"start": v(-204.2, -66.88) * mm, "mid": v(-199.7, -65.02) * mm, "end": v(-197.84, -60.53) * mm});
            skLineSegment(sketch, "E130.7", {"start": v(-204.2, -66.88) * mm, "end": v(-401.04, -66.88) * mm});
            skSolve(sketch);
        }
        {
            var Q0;
            Q0=makeQuery(id+"F14.imprint","IMPRINT",FACE,{"disambiguationData":[TD([[makeQuery(id+"F14.imprint","IMPRINT",EDGE,{"derivedFrom":sQuery(id+"F14.wireOp",EDGE,"E130.0")}),-1.0]])]});
            extrude(context, id + "F15", {"entities" : qUnion([Q0]), "operationType" : NewBodyOperationType.ADD, "depth" : 1.98 * mm});
        }
        {
            var Q0;
            Q0=makeQuery(id+"F15.opExtrude","CAP_FACE",FACE,{"disambiguationData":[OSD([sQuery(id+"F12.wireOp",EDGE,"E83.0"),sQuery(id+"F12.wireOp",EDGE,"E84.0"),sQuery(id+"F12.wireOp",EDGE,"E85.0"),sQuery(id+"F12.wireOp",EDGE,"E86.0"),sQuery(id+"F12.wireOp",EDGE,"E87.filletArc"),sQuery(id+"F12.wireOp",EDGE,"E88.filletArc"),sQuery(id+"F12.wireOp",EDGE,"E89.filletArc"),sQuery(id+"F12.wireOp",EDGE,"E90.filletArc"),sQuery(id+"F12.wireOp",EDGE,"E99"),sQuery(id+"F12.wireOp",EDGE,"E100"),sQuery(id+"F12.wireOp",EDGE,"E101"),sQuery(id+"F12.wireOp",EDGE,"E107"),sQuery(id+"F12.wireOp",EDGE,"E108.bottom"),sQuery(id+"F12.wireOp",EDGE,"E108.top"),sQuery(id+"F12.wireOp",EDGE,"E108.left"),sQuery(id+"F12.wireOp",EDGE,"E108.right"),sQuery(id+"F12.wireOp",EDGE,"E109.MirrorCS"),sQuery(id+"F12.wireOp",EDGE,"E110.MirrorCS"),sQuery(id+"F12.wireOp",EDGE,"E111.MirrorCS"),sQuery(id+"F12.wireOp",EDGE,"E112.MirrorCS"),sQuery(id+"F12.wireOp",EDGE,"E113.MirrorC"),sQuery(id+"F12.wireOp",EDGE,"E114.MirrorC"),sQuery(id+"F12.wireOp",EDGE,"E115.MirrorC"),sQuery(id+"F12.wireOp",EDGE,"E116.MirrorCS"),sQuery(id+"F12.wireOp",EDGE,"E117.MirrorCS"),sQuery(id+"F12.wireOp",EDGE,"E118.MirrorCS"),sQuery(id+"F12.wireOp",EDGE,"E119.MirrorCS"),sQuery(id+"F12.wireOp",EDGE,"E120.MirrorC"),sQuery(id+"F12.wireOp",EDGE,"E121.MirrorCS"),sQuery(id+"F12.wireOp",EDGE,"E122.MirrorCS"),sQuery(id+"F12.wireOp",EDGE,"E123.MirrorCS"),sQuery(id+"F12.wireOp",EDGE,"E124.MirrorCS"),sQuery(id+"F14.wireOp",EDGE,"E130.0"),sQuery(id+"F14.wireOp",EDGE,"E130.1"),sQuery(id+"F14.wireOp",EDGE,"E130.2"),sQuery(id+"F14.wireOp",EDGE,"E130.3"),sQuery(id+"F14.wireOp",EDGE,"E130.4"),sQuery(id+"F14.wireOp",EDGE,"E130.5"),sQuery(id+"F14.wireOp",EDGE,"E130.6"),sQuery(id+"F14.wireOp",EDGE,"E130.7")])],"isStart":false});
            var sketch = newSketch(context, id + "F16", { "sketchPlane" : qUnion([Q0])});
            skText(sketch, "E131", { "text": "M right", "fontName": "OpenSans-Regular.ttf"});
            const initialGuessF16  = {"E131": [-0.39388, 0.05085, 1, 0, 0.00453]};
            skSetInitialGuess(sketch, initialGuessF16);
            skSolve(sketch);
        }
        {
            var Q0;
            Q0 = qSketchRegion(id + "F16", true);
            extrude(context, id + "F17", {"entities" : qUnion([Q0]), "operationType" : NewBodyOperationType.REMOVE, "oppositeDirection" : true, "depth" : 0.4 * mm});
        }
        {
            var Q0;
            Q0=makeQuery(id+"F13.opExtrude","CAP_FACE",FACE,{"disambiguationData":[OSD([sQuery(id+"F12.wireOp",EDGE,"E82.0"),sQuery(id+"F12.wireOp",EDGE,"E82.1"),sQuery(id+"F12.wireOp",EDGE,"E82.2"),sQuery(id+"F12.wireOp",EDGE,"E82.3"),sQuery(id+"F12.wireOp",EDGE,"E82.4"),sQuery(id+"F12.wireOp",EDGE,"E82.5"),sQuery(id+"F12.wireOp",EDGE,"E82.6"),sQuery(id+"F12.wireOp",EDGE,"E82.7"),sQuery(id+"F12.wireOp",EDGE,"E83.0"),sQuery(id+"F12.wireOp",EDGE,"E84.0"),sQuery(id+"F12.wireOp",EDGE,"E85.0"),sQuery(id+"F12.wireOp",EDGE,"E86.0"),sQuery(id+"F12.wireOp",EDGE,"E87.filletArc"),sQuery(id+"F12.wireOp",EDGE,"E88.filletArc"),sQuery(id+"F12.wireOp",EDGE,"E89.filletArc"),sQuery(id+"F12.wireOp",EDGE,"E90.filletArc"),sQuery(id+"F12.wireOp",EDGE,"E99"),sQuery(id+"F12.wireOp",EDGE,"E100"),sQuery(id+"F12.wireOp",EDGE,"E101"),sQuery(id+"F12.wireOp",EDGE,"E107"),sQuery(id+"F12.wireOp",EDGE,"E108.bottom"),sQuery(id+"F12.wireOp",EDGE,"E108.top"),sQuery(id+"F12.wireOp",EDGE,"E108.left"),sQuery(id+"F12.wireOp",EDGE,"E108.right"),sQuery(id+"F12.wireOp",EDGE,"E109.MirrorCS"),sQuery(id+"F12.wireOp",EDGE,"E110.MirrorCS"),sQuery(id+"F12.wireOp",EDGE,"E111.MirrorCS"),sQuery(id+"F12.wireOp",EDGE,"E112.MirrorCS"),sQuery(id+"F12.wireOp",EDGE,"E113.MirrorC"),sQuery(id+"F12.wireOp",EDGE,"E114.MirrorC"),sQuery(id+"F12.wireOp",EDGE,"E115.MirrorC"),sQuery(id+"F12.wireOp",EDGE,"E116.MirrorCS"),sQuery(id+"F12.wireOp",EDGE,"E117.MirrorCS"),sQuery(id+"F12.wireOp",EDGE,"E118.MirrorCS"),sQuery(id+"F12.wireOp",EDGE,"E119.MirrorCS"),sQuery(id+"F12.wireOp",EDGE,"E120.MirrorC"),sQuery(id+"F12.wireOp",EDGE,"E121.MirrorCS"),sQuery(id+"F12.wireOp",EDGE,"E122.MirrorCS"),sQuery(id+"F12.wireOp",EDGE,"E123.MirrorCS"),sQuery(id+"F12.wireOp",EDGE,"E124.MirrorCS")])],"isStart":true});
            var sketch = newSketch(context, id + "F18", { "sketchPlane" : qUnion([Q0])});
            skArc(sketch, "E132.0", {"start": v(401.04, 41.07) * mm, "mid": v(405.53, 39.21) * mm, "end": v(407.4, 34.72) * mm});
            skLineSegment(sketch, "E132.1", {"start": v(407.4, 34.72) * mm, "end": v(407.4, -60.53) * mm});
            skLineSegment(sketch, "E132.2", {"start": v(401.04, 41.07) * mm, "end": v(204.2, 41.07) * mm});
            skArc(sketch, "E132.3", {"start": v(407.4, -60.53) * mm, "mid": v(405.53, -65.02) * mm, "end": v(401.04, -66.88) * mm});
            skArc(sketch, "E132.4", {"start": v(197.84, 34.72) * mm, "mid": v(199.7, 39.21) * mm, "end": v(204.2, 41.07) * mm});
            skLineSegment(sketch, "E132.5", {"start": v(197.84, 34.72) * mm, "end": v(197.84, -60.53) * mm});
            skArc(sketch, "E132.6", {"start": v(204.2, -66.88) * mm, "mid": v(199.7, -65.02) * mm, "end": v(197.84, -60.53) * mm});
            skLineSegment(sketch, "E132.7", {"start": v(401.04, -66.88) * mm, "end": v(204.2, -66.88) * mm});
            skArc(sketch, "E133.0", {"start": v(401.04, 37.9) * mm, "mid": v(403.29, 36.97) * mm, "end": v(404.22, 34.72) * mm});
            skLineSegment(sketch, "E133.1", {"start": v(404.22, 34.72) * mm, "end": v(404.22, -60.53) * mm});
            skLineSegment(sketch, "E133.2", {"start": v(401.04, 37.9) * mm, "end": v(204.2, 37.9) * mm});
            skArc(sketch, "E133.3", {"start": v(404.22, -60.53) * mm, "mid": v(403.29, -62.77) * mm, "end": v(401.04, -63.7) * mm});
            skArc(sketch, "E133.4", {"start": v(201.02, 34.72) * mm, "mid": v(201.95, 36.97) * mm, "end": v(204.2, 37.9) * mm});
            skLineSegment(sketch, "E133.5", {"start": v(201.02, 34.72) * mm, "end": v(201.02, -60.53) * mm});
            skArc(sketch, "E133.6", {"start": v(204.2, -63.7) * mm, "mid": v(201.95, -62.77) * mm, "end": v(201.02, -60.53) * mm});
            skLineSegment(sketch, "E133.7", {"start": v(401.04, -63.7) * mm, "end": v(204.2, -63.7) * mm});
            skSolve(sketch);
        }
        {
            var Q0;
            Q0 = qSketchRegion(id + "F18", true);
            extrude(context, id + "F19", {"entities" : qUnion([Q0]), "operationType" : NewBodyOperationType.ADD, "depth" : 0.8 * mm});
        }
        {
            var Q0;
            Q0=makeQuery(id+"F13.opExtrude","CAP_FACE",FACE,{"disambiguationData":[OSD([sQuery(id+"F12.wireOp",EDGE,"E82.0"),sQuery(id+"F12.wireOp",EDGE,"E82.1"),sQuery(id+"F12.wireOp",EDGE,"E82.2"),sQuery(id+"F12.wireOp",EDGE,"E82.3"),sQuery(id+"F12.wireOp",EDGE,"E82.4"),sQuery(id+"F12.wireOp",EDGE,"E82.5"),sQuery(id+"F12.wireOp",EDGE,"E82.6"),sQuery(id+"F12.wireOp",EDGE,"E82.7"),sQuery(id+"F12.wireOp",EDGE,"E83.0"),sQuery(id+"F12.wireOp",EDGE,"E84.0"),sQuery(id+"F12.wireOp",EDGE,"E85.0"),sQuery(id+"F12.wireOp",EDGE,"E86.0"),sQuery(id+"F12.wireOp",EDGE,"E87.filletArc"),sQuery(id+"F12.wireOp",EDGE,"E88.filletArc"),sQuery(id+"F12.wireOp",EDGE,"E89.filletArc"),sQuery(id+"F12.wireOp",EDGE,"E90.filletArc"),sQuery(id+"F12.wireOp",EDGE,"E99"),sQuery(id+"F12.wireOp",EDGE,"E100"),sQuery(id+"F12.wireOp",EDGE,"E101"),sQuery(id+"F12.wireOp",EDGE,"E107"),sQuery(id+"F12.wireOp",EDGE,"E108.bottom"),sQuery(id+"F12.wireOp",EDGE,"E108.top"),sQuery(id+"F12.wireOp",EDGE,"E108.left"),sQuery(id+"F12.wireOp",EDGE,"E108.right"),sQuery(id+"F12.wireOp",EDGE,"E109.MirrorCS"),sQuery(id+"F12.wireOp",EDGE,"E110.MirrorCS"),sQuery(id+"F12.wireOp",EDGE,"E111.MirrorCS"),sQuery(id+"F12.wireOp",EDGE,"E112.MirrorCS"),sQuery(id+"F12.wireOp",EDGE,"E113.MirrorC"),sQuery(id+"F12.wireOp",EDGE,"E114.MirrorC"),sQuery(id+"F12.wireOp",EDGE,"E115.MirrorC"),sQuery(id+"F12.wireOp",EDGE,"E116.MirrorCS"),sQuery(id+"F12.wireOp",EDGE,"E117.MirrorCS"),sQuery(id+"F12.wireOp",EDGE,"E118.MirrorCS"),sQuery(id+"F12.wireOp",EDGE,"E119.MirrorCS"),sQuery(id+"F12.wireOp",EDGE,"E120.MirrorC"),sQuery(id+"F12.wireOp",EDGE,"E121.MirrorCS"),sQuery(id+"F12.wireOp",EDGE,"E122.MirrorCS"),sQuery(id+"F12.wireOp",EDGE,"E123.MirrorCS"),sQuery(id+"F12.wireOp",EDGE,"E124.MirrorCS")])],"isStart":true});
            var sketch = newSketch(context, id + "F20", { "sketchPlane" : qUnion([Q0])});
            skLineSegment(sketch, "E134.bottom", {"start": v(234.36, 42.66) * mm, "end": v(272.46, 42.66) * mm});
            skLineSegment(sketch, "E134.top", {"start": v(234.36, 34.98) * mm, "end": v(272.46, 34.98) * mm});
            skLineSegment(sketch, "E134.left", {"start": v(234.36, 42.66) * mm, "end": v(234.36, 34.98) * mm});
            skLineSegment(sketch, "E134.right", {"start": v(272.46, 42.66) * mm, "end": v(272.46, 34.98) * mm});
            skLineSegment(sketch, "E135.bottom", {"start": v(234.36, -68.47) * mm, "end": v(272.46, -68.47) * mm});
            skLineSegment(sketch, "E135.top", {"start": v(234.36, -59.26) * mm, "end": v(272.46, -59.26) * mm});
            skLineSegment(sketch, "E135.left", {"start": v(234.36, -68.47) * mm, "end": v(234.36, -59.26) * mm});
            skLineSegment(sketch, "E135.right", {"start": v(272.46, -68.47) * mm, "end": v(272.46, -59.26) * mm});
            skLineSegment(sketch, "E136.bottom", {"start": v(332.78, -68.47) * mm, "end": v(368.75, -68.47) * mm});
            skLineSegment(sketch, "E136.top", {"start": v(332.78, -57.85) * mm, "end": v(368.75, -57.85) * mm});
            skLineSegment(sketch, "E136.left", {"start": v(332.78, -68.47) * mm, "end": v(332.78, -57.85) * mm});
            skLineSegment(sketch, "E136.right", {"start": v(368.75, -68.47) * mm, "end": v(368.75, -57.85) * mm});
            skSolve(sketch);
        }
        {
            var Q0;
            Q0 = qSketchRegion(id + "F20", true);
            extrude(context, id + "F21", {"entities" : qUnion([Q0]), "operationType" : NewBodyOperationType.REMOVE, "oppositeDirection" : true, "depth" : 0.8 * mm});
        }
    });
